# Revit family: PGL8
name_source: partatom
category: Lighting Fixtures
units: mm (PartAtom-declared; Revit-internal decimal feet)

## family parameters
Cut with Voids When Loaded = No
Host = Face
Light Source = Yes
OmniClass Number = 23.80.70.00
OmniClass Title = Lighting
Part Type = Normal
Room Calculation Point = No
Round Connector Dimension = Use Diameter
Shared = No

## types (1)
- PGL8
    Assembly Code = D5020200
    Certifications = UL listed
    Color Filter = 16777215
    Default Elevation = 48 "
    Description = LED Parking Garage Luminaire
    Dimming Interface = 0-10V
    Dimming Lamp Color Temperature Shift = <None>
    Distribution = Type V Concentrated, Type V Square, Type V Rectangular, Asymmetric
    Emit Shape Visible in Rendering = No
    Emit from Circle Diameter = 14 "
    Features = Patent Pending edge lit, drop lens optic
• The PGL8 offers exceptional uniformity
and visual comfort with four standard
distribution patterns
• Multiple control options available for a intelligent
parking garage lighting solution
• Integrnal sensors, battery backup and uplight
    Glass = Paint - Matte White
    Housing = Metal-Galvanized_Steel
    IP Rating = IP 65
    Lamp = LED
    Manufacturer = KIM LIGHTING
    Model = PGL8
    Photometric Web File = L031903201 PGL8-128L130-5K7-SM-T5W-UNV-WH (S-LITE) Full reflector Shield_600mA.IES
    Power Factor = 0.90
    Tilt Angle = -90.00°
    Type Comments = Light Fixture
    URL = https://www.currentlighting.com
    Warranty = 5 Years Limited Warranty

## geometry (parser evidence)
native form markers: Sweep x3
no freeform markers — native parametric forms only
